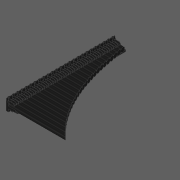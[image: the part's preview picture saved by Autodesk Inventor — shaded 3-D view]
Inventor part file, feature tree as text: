
AUTODESK INVENTOR PART (.ipt)
format: ipt  version: 2020 (Build 240168000, 168)  size: 2,511,360 bytes
history: native  units: in
note: dims shown in document units (in); Inventor stores cm internally (conversion verified against a paired STEP export)
features: other x24, extrude x15, pattern_linear x3, loft x2, fillet x1, sketch x1
ambient origin geometry x8: Origin, YZ Plane, XZ Plane, XY Plane, X Axis, Y Axis, Z Axis, Center Point
bodies: Solid1 (feature_tree)
feature tree (46):
  other  "CrossSection1"
  other  "Vertical Midplane"
  other  "Horizontal Midplane"
  extrude  "Block"  Depth=11.8307in
  extrude  "Hinge Protrusion"  Depth=11.8307in TaperAngle=0.0deg
  other  "Resonator Profile"
  extrude  "Resonator"  Depth=11.8307in
  extrude  "Resonator Cut"  TaperAngle=0.0deg  [1 undecoded]
  extrude  "Duct Cavity"  Depth=11.8307in
  other  "Duct Entrance Loft Plane"
  loft  "Duct Entrance"
  other  "Fitting"
  extrude  "Slit"  Depth=11.8307in
  extrude  "Edge Cut"  Depth=11.8307in
  other  "Edge Plane"
  other  "Edge Sketch"
  loft  "Edge Loft"
  extrude  "Edge"  Depth=11.8307in
  other  "Edge Cut Plane"
  pattern_linear  "Channel Repetition"  Spacing1=0.5512in  [1 undecoded]
  extrude  "Edge Length Cut"  Depth=0.2362in TaperAngle=0.0deg
  other  "Tube Length Curve"
  extrude  "Tube Length Cut"  Depth=0.2461in
  extrude  "Whistle Walls"  Depth=11.8307in
  fillet  "Whistle Wall Fillet"  Radius=0.1245in
  pattern_linear  "Whistle Wall Repetition"  Spacing1=0.1528in  [1 undecoded]
  other  "End Cap Tidying Plane"
  other  "End Cap Tidying Sketch"
  extrude  "End Caps"  Depth=0.2461in
  extrude  "End Cap Tidying"  Depth=0.3937in
  extrude  "Block Fix"  Depth=0.2362in TaperAngle=0.0deg
  pattern_linear  "End Cap Tidying Repetition"  Spacing1=0.0197in  [1 undecoded]
  extrude  "End Cap Tidying (edges)"  Depth=11.8307in
  other  "Block Profile"
  other  "Fitting Sketch"
  other  "Duct Cavity Profile"
  other  "Duct Entrance Loft From"
  other  "Slit Sketch"
  other  "Hinge Protrusion Sketch"
  other  "Edge Cut Sketch"
  other  "Edges3"
  other  "Edge Length Curve"
  sketch  "Sketch19"  dims[d6=0.0in d7=9.8425in d9=0.4724in d20=0.3153in d21=0.0in d58=0.4921in d59=0.0in d61=0.4921in d62=2.3498in d63=0.0in d70=0.1969in d71=0.1292in d80=90.0deg d100=0.2151in d104=0.5512in d105=0.2362in d106=0.0in d109=0.2461in d111=0.1528in d112=0.1245in d114=0.1528in d115=0.2461in d118=0.3937in d141=0.2362in d142=0.0in d148=0.0197in d150=0.2559in d151=0.8858in d152=0.4921in d154=0.0in d160=0.1969in d161=0.0in d162=0.2461in d163=0.2362in d165=0.2461in d166=0.2461in d167=0.0in d171=0.2362in d174=0.4921in d175=0.4528in d176=0.0in d177=90.0deg d178=0.0in d179=90.0deg d185=0.3273in d186=0.0in d189=0.1931in d190=28.3465in d191=38.2054in d198=0.0803in d199=0.0in d200=0.0197in d201=0.0787in d202=-0.125in d203=0.7874in d206=0.2559in d207=0.5241in d209=0.0in d211=9.8425in d213=0.4724in d214=0.2362in d216=0.4528in d217=0.4921in d222=0.0236in d223=0.8058in d229=0.4921in d230=0.0in d234=0.4724in d235=0.4921in d237=0.2461in d239=1.4483in d240=0.0in d241=9.8425in d243=0.4724in d246=0.0394in d247=0.7043in d248=0.0in d249=0.2461in d250=11.8209in d251=0.0098in d252=28.3465in d253=38.2054in d254=28.3465in d255=38.2054in d256=-0.1181in d257=0.2362in d258=0.2151in d259=0.2461in d260=0.1245in d261=0.0in d262=90.0deg d263=0.0in d264=90.0deg d265=11.8307in d266=6.2114in d267=0.9843in d268=0.0in d137=0.0197in d138=0.0344in d139=0.0197in d140=0.0344in d208=0.0197in d269=0.0197in d270=0.0344in]
  other  "2D Equation Curve10"
  other  "2D Equation Curve11"
  other  "Duct Entrance Loft To"
note: 4 required parameter values undecoded (feature->parameter linkage not recoverable at this tier; creation-order binding heuristic only, values carry confidence <= 0.55)
